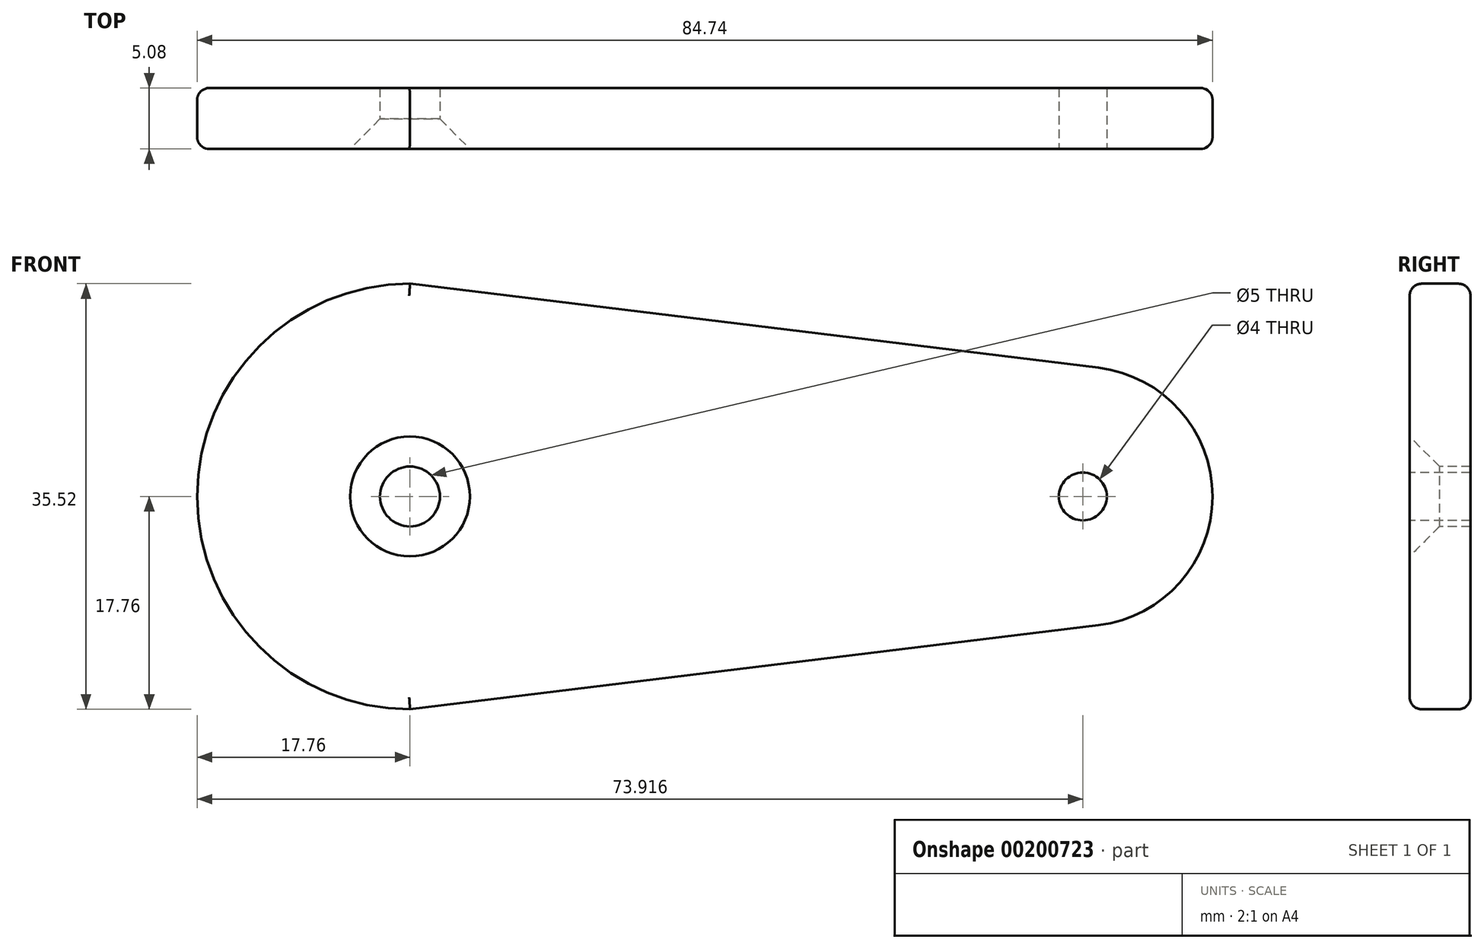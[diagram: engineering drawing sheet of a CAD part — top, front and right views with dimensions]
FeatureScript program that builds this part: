
annotation { "Feature Type Name" : "Feature", "Feature Type Description" : "" }
export const myFeature = defineFeature(function(context is Context, id is Id, definition is map)
    precondition{}
    {
        {
            var Q0;
            Q0=qCreatedBy(makeId("Front.planeOp"),FACE);
            var sketch = newSketch(context, id + "F0", { "sketchPlane" : qUnion([Q0])});
            skArc(sketch, "E0", {"start": v(4.27, 17.24) * mm, "mid": v(-17.76, 0) * mm, "end": v(4.27, -17.24) * mm});
            skArc(sketch, "E1", {"start": v(57.47, -10.75) * mm, "mid": v(66.98, 0) * mm, "end": v(57.47, 10.75) * mm});
            skLineSegment(sketch, "E2", {"start": v(0, 17.76) * mm, "end": v(57.47, 10.75) * mm});
            skLineSegment(sketch, "E3", {"start": v(0, -17.76) * mm, "end": v(57.47, -10.75) * mm});
            skSolve(sketch);
        }
        {
            var Q0;
            {var subQ3=sQuery(id+"F0.wireOp",EDGE,"E1");Q0=makeQuery(id+"F0.imprint","IMPRINT",FACE,{"disambiguationData":[TD([[makeQuery(id+"F0.imprint","IMPRINT",EDGE,{"derivedFrom":subQ3}),1.0]])]});}
            extrude(context, id + "F1", {"entities" : qUnion([Q0]), "depth" : 5.08 * mm});
        }
        {
            var Q0;
            Q0=makeQuery(id+"F1.opExtrude","CAP_FACE",FACE,{"disambiguationData":[OSD([sQuery(id+"F0.wireOp",EDGE,"E0"),sQuery(id+"F0.wireOp",EDGE,"E1"),sQuery(id+"F0.wireOp",EDGE,"E2"),sQuery(id+"F0.wireOp",EDGE,"E3")])],"isStart":false});
            fillet(context, id + "F2", {"entities" : qUnion([Q0]), "radius" : 1 * mm, "tangentPropagation" : true, "allowEdgeOverflow" : false});
        }
        {
            var Q0;
            Q0=makeQuery(id+"F1.opExtrude","CAP_FACE",FACE,{"disambiguationData":[OSD([sQuery(id+"F0.wireOp",EDGE,"E0"),sQuery(id+"F0.wireOp",EDGE,"E1"),sQuery(id+"F0.wireOp",EDGE,"E2"),sQuery(id+"F0.wireOp",EDGE,"E3")])],"isStart":true});
            fillet(context, id + "F3", {"entities" : qUnion([Q0]), "radius" : 1 * mm, "tangentPropagation" : true, "allowEdgeOverflow" : false});
        }
        {
            var Q0;
            Q0=makeQuery(id+"F1.opExtrude","CAP_FACE",FACE,{"disambiguationData":[OSD([sQuery(id+"F0.wireOp",EDGE,"E0"),sQuery(id+"F0.wireOp",EDGE,"E1"),sQuery(id+"F0.wireOp",EDGE,"E2"),sQuery(id+"F0.wireOp",EDGE,"E3")])],"isStart":false});
            var sketch = newSketch(context, id + "F4", { "sketchPlane" : qUnion([Q0])});
            skPoint(sketch, "E4", {"position": v(0, 0) * mm});
            skPoint(sketch, "E5", {"position": v(56.16, 0) * mm});
            skLineSegment(sketch, "E6", {"start": v(0, 0) * mm, "end": v(56.16, 0) * mm, "construction": true});
            skSolve(sketch);
        }
        {
            var Q0;
            Q0=sQuery(id+"F4.wireOp",VERTEX,"E4");
            var Q1;
            Q1=makeQuery(id+"F1.opExtrude","SWEPT_BODY",BODY,{"disambiguationData":[OSD([sQuery(id+"F0.wireOp",EDGE,"E0"),sQuery(id+"F0.wireOp",EDGE,"E1"),sQuery(id+"F0.wireOp",EDGE,"E2"),sQuery(id+"F0.wireOp",EDGE,"E3")])]});
            hole(context, id + "F5", {"style" : HoleStyle.C_SINK, "endStyle" : HoleEndStyle.THROUGH, "holeDiameter" : 5 * mm, "cSinkDiameter" : 10 * mm, "cSinkAngle" : 90 * degree, "locations" : qUnion([Q0]), "scope" : qUnion([Q1]), "isTappedThrough" : true});
        }
        {
            var Q0;
            Q0=sQuery(id+"F4.wireOp",VERTEX,"E5");
            var Q1;
            Q1=makeQuery(id+"F1.opExtrude","SWEPT_BODY",BODY,{"disambiguationData":[OSD([sQuery(id+"F0.wireOp",EDGE,"E0"),sQuery(id+"F0.wireOp",EDGE,"E1"),sQuery(id+"F0.wireOp",EDGE,"E2"),sQuery(id+"F0.wireOp",EDGE,"E3")])]});
            hole(context, id + "F6", {"style" : HoleStyle.SIMPLE, "endStyle" : HoleEndStyle.THROUGH, "holeDiameter" : 4 * mm, "locations" : qUnion([Q0]), "scope" : qUnion([Q1]), "isTappedThrough" : true});
        }
    });
